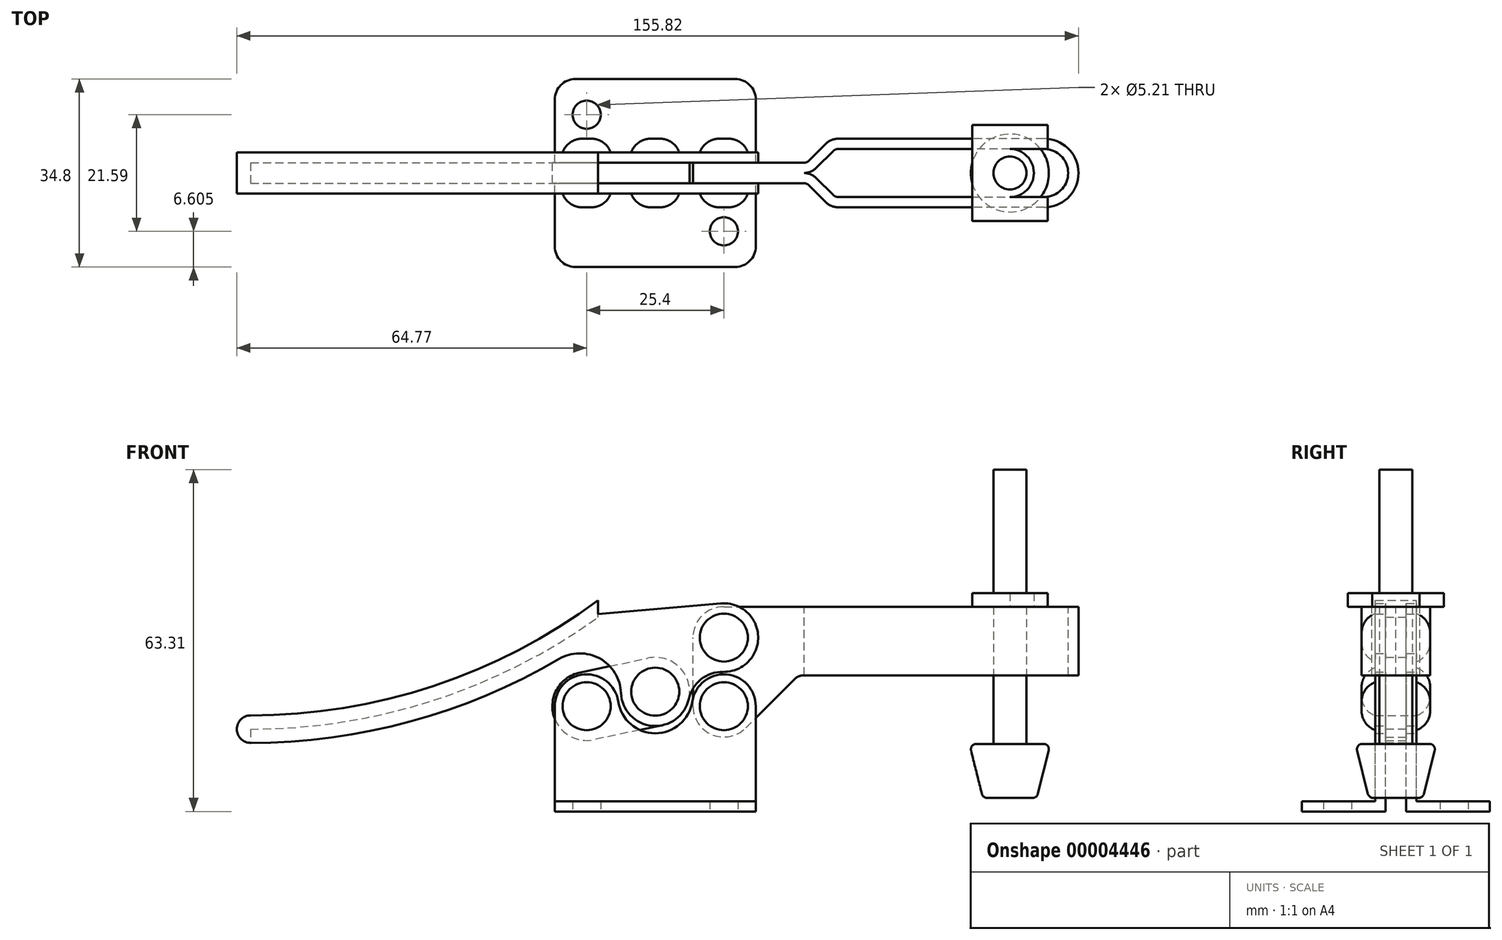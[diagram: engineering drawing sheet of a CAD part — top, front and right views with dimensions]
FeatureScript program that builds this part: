
annotation { "Feature Type Name" : "Feature", "Feature Type Description" : "" }
export const myFeature = defineFeature(function(context is Context, id is Id, definition is map)
    precondition{}
    {
        {
            var Q0;
            Q0=qCreatedBy(makeId("Front.planeOp"),FACE);
            var sketch = newSketch(context, id + "F0", { "sketchPlane" : qUnion([Q0])});
            skLineSegment(sketch, "E0", {"start": v(0, 0) * mm, "end": v(-18.6, 0) * mm});
            skLineSegment(sketch, "E1", {"start": v(-18.6, 0) * mm, "end": v(-18.6, 19.5) * mm});
            skArc(sketch, "E2", {"start": v(-18.6, 19.5) * mm, "mid": v(-13.14, 25.38) * mm, "end": v(-6.86, 20.38) * mm});
            skArc(sketch, "E3", {"start": v(-6.86, 20.38) * mm, "mid": v(-4.52, 16.16) * mm, "end": v(0, 14.48) * mm});
            skArc(sketch, "E4.0.MirrorCS", {"start": v(6.86, 20.38) * mm, "mid": v(4.52, 16.16) * mm, "end": v(0, 14.48) * mm});
            skLineSegment(sketch, "E4.1.MirrorCS", {"start": v(0, 0) * mm, "end": v(18.6, 0) * mm});
            skLineSegment(sketch, "E4.2.MirrorCS", {"start": v(18.6, 0) * mm, "end": v(18.6, 19.5) * mm});
            skArc(sketch, "E4.3.MirrorCS", {"start": v(18.6, 19.5) * mm, "mid": v(13.14, 25.38) * mm, "end": v(6.86, 20.38) * mm});
            skCircle(sketch, "E5", {"center": v(-12.7, 19.5) * mm, "radius": 3.81 * mm});
            skCircle(sketch, "E6.0.MirrorC", {"center": v(12.7, 19.5) * mm, "radius": 3.81 * mm});
            skLineSegment(sketch, "E7", {"start": v(-18.6, 1.9) * mm, "end": v(18.6, 1.9) * mm});
            skSolve(sketch);
        }
        {
            var Q0;
            Q0 = qSketchRegion(id + "F0", true);
            extrude(context, id + "F1", {"entities" : qUnion([Q0]), "endBound" : BoundingType.SYMMETRIC, "depth" : 7.62 * mm});
        }
        {
            var Q0;
            {var subQ2=sQuery(id+"F0.wireOp",EDGE,"E0");Q0=makeQuery(id+"F0.imprint","IMPRINT",FACE,{"disambiguationData":[TD([[makeQuery(id+"F0.imprint","IMPRINT",EDGE,{"derivedFrom":subQ2}),-1.0]])]});}
            extrude(context, id + "F2", {"entities" : qUnion([Q0]), "operationType" : NewBodyOperationType.ADD, "endBound" : BoundingType.SYMMETRIC, "depth" : 34.8 * mm});
        }
        {
            var Q0;
            Q0 = qSketchRegion(id + "F0", true);
            extrude(context, id + "F3", {"entities" : qUnion([Q0]), "operationType" : NewBodyOperationType.REMOVE, "endBound" : BoundingType.SYMMETRIC, "oppositeDirection" : true, "depth" : 3.8 * mm});
        }
        {
            var Q0;
            Q0=qCreatedBy(makeId("Top.planeOp"),FACE);
            var sketch = newSketch(context, id + "F4", { "sketchPlane" : qUnion([Q0])});
            skCircle(sketch, "E8", {"center": v(-12.7, 10.8) * mm, "radius": 2.6 * mm});
            skArc(sketch, "E9", {"start": v(-14.8, 17.4) * mm, "mid": v(-17.49, 16.28) * mm, "end": v(-18.6, 13.59) * mm});
            skLineSegment(sketch, "E10", {"start": v(-18.6, 13.59) * mm, "end": v(-18.6, 17.4) * mm});
            skLineSegment(sketch, "E11", {"start": v(-18.6, 17.4) * mm, "end": v(-14.8, 17.4) * mm});
            skCircle(sketch, "E12.0.MirrorC", {"center": v(12.7, 10.8) * mm, "radius": 2.6 * mm});
            skLineSegment(sketch, "E12.1.MirrorCS", {"start": v(18.6, 17.4) * mm, "end": v(14.8, 17.4) * mm});
            skLineSegment(sketch, "E12.2.MirrorCS", {"start": v(18.6, 13.59) * mm, "end": v(18.6, 17.4) * mm});
            skArc(sketch, "E12.3.MirrorCS", {"start": v(14.8, 17.4) * mm, "mid": v(17.49, 16.28) * mm, "end": v(18.6, 13.59) * mm});
            skLineSegment(sketch, "E13.0.MirrorCS", {"start": v(-18.6, -13.59) * mm, "end": v(-18.6, -17.4) * mm});
            skArc(sketch, "E13.1.MirrorCS", {"start": v(-14.8, -17.4) * mm, "mid": v(-17.49, -16.28) * mm, "end": v(-18.6, -13.59) * mm});
            skCircle(sketch, "E13.2.MirrorC", {"center": v(12.7, -10.8) * mm, "radius": 2.6 * mm});
            skCircle(sketch, "E13.3.MirrorC", {"center": v(-12.7, -10.8) * mm, "radius": 2.6 * mm});
            skArc(sketch, "E13.4.MirrorCS", {"start": v(14.8, -17.4) * mm, "mid": v(17.49, -16.28) * mm, "end": v(18.6, -13.59) * mm});
            skLineSegment(sketch, "E13.5.MirrorCS", {"start": v(-18.6, -17.4) * mm, "end": v(-14.8, -17.4) * mm});
            skLineSegment(sketch, "E13.6.MirrorCS", {"start": v(18.6, -17.4) * mm, "end": v(14.8, -17.4) * mm});
            skLineSegment(sketch, "E13.7.MirrorCS", {"start": v(18.6, -13.59) * mm, "end": v(18.6, -17.4) * mm});
            skSolve(sketch);
        }
        {
            var Q0;
            Q0=makeQuery(id+"F4.imprint","IMPRINT",FACE,{"disambiguationData":[TD([[makeQuery(id+"F4.imprint","IMPRINT",EDGE,{"derivedFrom":sQuery(id+"F4.wireOp",EDGE,"E8")}),1.0]])]});
            var Q1;
            Q1=makeQuery(id+"F4.imprint","IMPRINT",FACE,{"disambiguationData":[TD([[makeQuery(id+"F4.imprint","IMPRINT",EDGE,{"derivedFrom":sQuery(id+"F4.wireOp",EDGE,"E9")}),-1.0]])]});
            var Q2;
            Q2=makeQuery(id+"F4.imprint","IMPRINT",FACE,{"disambiguationData":[TD([[makeQuery(id+"F4.imprint","IMPRINT",EDGE,{"derivedFrom":sQuery(id+"F4.wireOp",EDGE,"E12.0.MirrorC")}),-1.0]])]});
            var Q3;
            Q3=makeQuery(id+"F4.imprint","IMPRINT",FACE,{"disambiguationData":[TD([[makeQuery(id+"F4.imprint","IMPRINT",EDGE,{"derivedFrom":sQuery(id+"F4.wireOp",EDGE,"E12.1.MirrorCS")}),1.0]])]});
            var Q4;
            Q4=makeQuery(id+"F4.imprint","IMPRINT",FACE,{"disambiguationData":[TD([[makeQuery(id+"F4.imprint","IMPRINT",EDGE,{"derivedFrom":sQuery(id+"F4.wireOp",EDGE,"E13.2.MirrorC")}),1.0]])]});
            var Q5;
            Q5=makeQuery(id+"F4.imprint","IMPRINT",FACE,{"disambiguationData":[TD([[makeQuery(id+"F4.imprint","IMPRINT",EDGE,{"derivedFrom":sQuery(id+"F4.wireOp",EDGE,"E13.4.MirrorCS")}),-1.0]])]});
            var Q6;
            Q6=makeQuery(id+"F4.imprint","IMPRINT",FACE,{"disambiguationData":[TD([[makeQuery(id+"F4.imprint","IMPRINT",EDGE,{"derivedFrom":sQuery(id+"F4.wireOp",EDGE,"E13.0.MirrorCS")}),1.0]])]});
            var Q7;
            Q7=makeQuery(id+"F4.imprint","IMPRINT",FACE,{"disambiguationData":[TD([[makeQuery(id+"F4.imprint","IMPRINT",EDGE,{"derivedFrom":sQuery(id+"F4.wireOp",EDGE,"E13.3.MirrorC")}),-1.0]])]});
            extrude(context, id + "F5", {"entities" : qUnion([Q0, Q1, Q2, Q3, Q4, Q5, Q6, Q7]), "operationType" : NewBodyOperationType.REMOVE, "endBound" : BoundingType.THROUGH_ALL, "depth" : 25.4 * mm});
        }
        {
            var Q0;
            Q0=qCreatedBy(makeId("Front.planeOp"),FACE);
            var sketch = newSketch(context, id + "F6", { "sketchPlane" : qUnion([Q0])});
            skCircle(sketch, "E14", {"center": v(12.7, 19.5) * mm, "radius": 5.72 * mm});
            skLineSegment(sketch, "E15", {"start": v(6.98, 19.5) * mm, "end": v(6.98, 32.2) * mm});
            skCircle(sketch, "E16", {"center": v(12.7, 32.2) * mm, "radius": 5.72 * mm});
            skLineSegment(sketch, "E17", {"start": v(12.7, 37.9) * mm, "end": v(75.8, 37.9) * mm});
            skLineSegment(sketch, "E18", {"start": v(16.74, 15.45) * mm, "end": v(25.75, 24.47) * mm});
            skArc(sketch, "E19", {"start": v(25.75, 24.47) * mm, "mid": v(26.58, 25.02) * mm, "end": v(27.55, 25.2) * mm});
            skLineSegment(sketch, "E20", {"start": v(27.55, 25.2) * mm, "end": v(75.8, 25.2) * mm});
            skLineSegment(sketch, "E21", {"start": v(27.55, 25.2) * mm, "end": v(27.55, 37.9) * mm});
            skArc(sketch, "E22", {"start": v(75.8, 25.2) * mm, "mid": v(77.6, 25.95) * mm, "end": v(78.35, 27.75) * mm});
            skArc(sketch, "E23", {"start": v(75.8, 37.9) * mm, "mid": v(77.6, 37.17) * mm, "end": v(78.35, 35.37) * mm});
            skLineSegment(sketch, "E24", {"start": v(78.35, 35.37) * mm, "end": v(78.35, 27.75) * mm});
            skCircle(sketch, "E25", {"center": v(-12.7, 19.5) * mm, "radius": 3.81 * mm});
            skCircle(sketch, "E26", {"center": v(0, 22.18) * mm, "radius": 3.81 * mm});
            skCircle(sketch, "E27", {"center": v(-12.7, 19.5) * mm, "radius": 6.35 * mm});
            skCircle(sketch, "E28", {"center": v(0, 22.18) * mm, "radius": 6.35 * mm});
            skLineSegment(sketch, "E29", {"start": v(-14.01, 25.7) * mm, "end": v(-1.31, 28.4) * mm});
            skLineSegment(sketch, "E30", {"start": v(1.31, 15.97) * mm, "end": v(-11.39, 13.28) * mm});
            skSolve(sketch);
        }
        {
            var Q0;
            {var subQ0=sQuery(id+"F6.wireOp",EDGE,"E14");var subQ2=makeQuery(id+"F6.imprint","INTERSECT",VERTEX,{"derivedFrom":[subQ0,sQuery(id+"F6.wireOp",EDGE,"E15")]});Q0=makeQuery(id+"F6.imprint","IMPRINT",FACE,{"disambiguationData":[TD([[makeQuery(id+"F6.imprint","IMPRINT",EDGE,{"disambiguationData":[TD([[subQ2,-1.0]])],"derivedFrom":subQ0}),1.0]])]});}
            var Q1;
            {var subQ0=sQuery(id+"F6.wireOp",EDGE,"E16");var subQ2=makeQuery(id+"F6.imprint","INTERSECT",VERTEX,{"derivedFrom":[sQuery(id+"F6.wireOp",EDGE,"E15"),subQ0]});Q1=makeQuery(id+"F6.imprint","IMPRINT",FACE,{"disambiguationData":[TD([[makeQuery(id+"F6.imprint","IMPRINT",EDGE,{"disambiguationData":[TD([[subQ2,1.0]])],"derivedFrom":subQ0}),1.0]])]});}
            var Q2;
            {var subQ5=sQuery(id+"F6.wireOp",EDGE,"E15");Q2=makeQuery(id+"F6.imprint","IMPRINT",FACE,{"disambiguationData":[TD([[makeQuery(id+"F6.imprint","IMPRINT",EDGE,{"derivedFrom":subQ5}),-1.0]])]});}
            var Q3;
            {var subQ1=sQuery(id+"F6.wireOp",EDGE,"E29");Q3=makeQuery(id+"F6.imprint","IMPRINT",FACE,{"disambiguationData":[TD([[makeQuery(id+"F6.imprint","IMPRINT",EDGE,{"derivedFrom":subQ1}),-1.0]])]});}
            var Q4;
            Q4=makeQuery(id+"F6.imprint","IMPRINT",FACE,{"disambiguationData":[TD([[makeQuery(id+"F6.imprint","IMPRINT",EDGE,{"derivedFrom":sQuery(id+"F6.wireOp",EDGE,"E26")}),-1.0]])]});
            var Q5;
            Q5=makeQuery(id+"F6.imprint","IMPRINT",FACE,{"disambiguationData":[TD([[makeQuery(id+"F6.imprint","IMPRINT",EDGE,{"derivedFrom":sQuery(id+"F6.wireOp",EDGE,"E25")}),-1.0]])]});
            extrude(context, id + "F7", {"entities" : qUnion([Q0, Q1, Q2, Q3, Q4, Q5]), "operationType" : NewBodyOperationType.ADD, "endBound" : BoundingType.SYMMETRIC, "depth" : 3.8 * mm});
        }
        {
            var Q0;
            Q0=makeQuery(id+"F7.opExtrude","SWEPT_FACE",FACE,{"disambiguationData":[OSD([sQuery(id+"F6.wireOp",EDGE,"E17")])]});
            var sketch = newSketch(context, id + "F8", { "sketchPlane" : qUnion([Q0])});
            skLineSegment(sketch, "E31", {"start": v(12.7, 1.9) * mm, "end": v(27.55, 1.9) * mm});
            skArc(sketch, "E32", {"start": v(27.55, 1.9) * mm, "mid": v(28.04, 2) * mm, "end": v(28.45, 2.28) * mm});
            skLineSegment(sketch, "E33", {"start": v(27.55, 0) * mm, "end": v(12.7, 0) * mm});
            skArc(sketch, "E34", {"start": v(27.55, 0) * mm, "mid": v(28.76, 0.24) * mm, "end": v(29.8, 0.93) * mm});
            skLineSegment(sketch, "E35", {"start": v(28.45, 2.28) * mm, "end": v(31.6, 5.42) * mm});
            skLineSegment(sketch, "E36", {"start": v(29.8, 0.93) * mm, "end": v(32.94, 4.07) * mm});
            skLineSegment(sketch, "E37", {"start": v(33.84, 4.44) * mm, "end": v(72, 4.44) * mm});
            skLineSegment(sketch, "E38", {"start": v(72, 6.35) * mm, "end": v(33.84, 6.35) * mm});
            skArc(sketch, "E39", {"start": v(32.94, 4.07) * mm, "mid": v(33.35, 4.35) * mm, "end": v(33.84, 4.44) * mm});
            skArc(sketch, "E40", {"start": v(31.6, 5.42) * mm, "mid": v(32.62, 6.1) * mm, "end": v(33.84, 6.35) * mm});
            skArc(sketch, "E41", {"start": v(72, 4.44) * mm, "mid": v(75.14, 3.14) * mm, "end": v(76.44, 0) * mm});
            skArc(sketch, "E42", {"start": v(72, 6.35) * mm, "mid": v(76.49, 4.5) * mm, "end": v(78.35, 0) * mm});
            skLineSegment(sketch, "E43", {"start": v(76.44, 0) * mm, "end": v(78.35, 0) * mm});
            skArc(sketch, "E44.0.MirrorCS", {"start": v(72, -4.45) * mm, "mid": v(75.14, -3.14) * mm, "end": v(76.44, 0) * mm});
            skArc(sketch, "E44.1.MirrorCS", {"start": v(31.6, -5.42) * mm, "mid": v(32.62, -6.1) * mm, "end": v(33.84, -6.35) * mm});
            skLineSegment(sketch, "E44.3.MirrorCS", {"start": v(29.8, -0.93) * mm, "end": v(32.94, -4.07) * mm});
            skArc(sketch, "E44.4.MirrorCS", {"start": v(72, -6.35) * mm, "mid": v(76.49, -4.5) * mm, "end": v(78.35, 0) * mm});
            skArc(sketch, "E44.5.MirrorCS", {"start": v(27.55, -1.9) * mm, "mid": v(28.04, -2) * mm, "end": v(28.45, -2.28) * mm});
            skLineSegment(sketch, "E44.6.MirrorCS", {"start": v(33.84, -4.44) * mm, "end": v(72, -4.44) * mm});
            skLineSegment(sketch, "E44.7.MirrorCS", {"start": v(72, -6.35) * mm, "end": v(33.84, -6.35) * mm});
            skLineSegment(sketch, "E44.8.MirrorCS", {"start": v(28.45, -2.28) * mm, "end": v(31.6, -5.42) * mm});
            skArc(sketch, "E44.9.MirrorCS", {"start": v(32.94, -4.07) * mm, "mid": v(33.35, -4.35) * mm, "end": v(33.84, -4.44) * mm});
            skArc(sketch, "E44.10.MirrorCS", {"start": v(27.55, 0) * mm, "mid": v(28.76, -0.24) * mm, "end": v(29.8, -0.93) * mm});
            skSolve(sketch);
        }
        {
            var Q0;
            Q0=makeQuery(id+"F8.imprint","IMPRINT",FACE,{"disambiguationData":[TD([[makeQuery(id+"F8.imprint","IMPRINT",EDGE,{"derivedFrom":sQuery(id+"F8.wireOp",EDGE,"E44.0.MirrorCS")}),-1.0]])]});
            var Q1;
            {var subQ2=sQuery(id+"F8.wireOp",EDGE,"E32");Q1=makeQuery(id+"F8.imprint","IMPRINT",FACE,{"disambiguationData":[TD([[makeQuery(id+"F8.imprint","IMPRINT",EDGE,{"derivedFrom":subQ2}),-1.0]])]});}
            var Q2;
            Q2=makeQuery(id+"F8.imprint","IMPRINT",FACE,{"disambiguationData":[TD([[makeQuery(id+"F8.imprint","IMPRINT",EDGE,{"derivedFrom":sQuery(id+"F8.wireOp",EDGE,"E34")}),-1.0]])]});
            extrude(context, id + "F9", {"entities" : qUnion([Q0, Q1, Q2]), "operationType" : NewBodyOperationType.ADD, "oppositeDirection" : true, "depth" : 12.7 * mm});
        }
        {
            var Q0;
            Q0=makeQuery(id+"F8.imprint","IMPRINT",FACE,{"disambiguationData":[TD([[makeQuery(id+"F8.imprint","IMPRINT",EDGE,{"derivedFrom":sQuery(id+"F8.wireOp",EDGE,"E34")}),-1.0]])]});
            extrude(context, id + "F10", {"entities" : qUnion([Q0]), "operationType" : NewBodyOperationType.REMOVE, "endBound" : BoundingType.THROUGH_ALL, "oppositeDirection" : true, "depth" : 25.4 * mm});
        }
        {
            var Q0;
            Q0=qCreatedBy(makeId("Front.planeOp"),FACE);
            var sketch = newSketch(context, id + "F11", { "sketchPlane" : qUnion([Q0])});
            skCircle(sketch, "E45", {"center": v(12.7, 32.2) * mm, "radius": 6.35 * mm});
            skCircle(sketch, "E46", {"center": v(0, 22.18) * mm, "radius": 6.35 * mm});
            skArc(sketch, "E47", {"start": v(12.56, 25.85) * mm, "mid": v(8.48, 24.48) * mm, "end": v(6.2, 20.84) * mm});
            skArc(sketch, "E48", {"start": v(-6.35, 21.94) * mm, "mid": v(-10.3, 28.33) * mm, "end": v(-17.82, 28.22) * mm});
            skArc(sketch, "E49", {"start": v(-17.82, 28.22) * mm, "mid": v(-45.34, 16.65) * mm, "end": v(-74.93, 12.7) * mm});
            skArc(sketch, "E50", {"start": v(-74.93, 12.7) * mm, "mid": v(-77.47, 15.24) * mm, "end": v(-74.93, 17.78) * mm});
            skArc(sketch, "E51", {"start": v(-74.93, 17.78) * mm, "mid": v(-41.06, 23.24) * mm, "end": v(-10.63, 39.07) * mm});
            skLineSegment(sketch, "E52", {"start": v(12.15, 38.52) * mm, "end": v(-10.63, 36.53) * mm});
            skLineSegment(sketch, "E53", {"start": v(-10.63, 36.53) * mm, "end": v(-10.63, 39.07) * mm});
            skArc(sketch, "E54", {"start": v(-74.93, 15.24) * mm, "mid": v(-41.16, 20.54) * mm, "end": v(-10.63, 35.92) * mm});
            skLineSegment(sketch, "E55", {"start": v(-10.63, 36.53) * mm, "end": v(-10.63, 35.92) * mm});
            skLineSegment(sketch, "E56", {"start": v(-74.93, 15.24) * mm, "end": v(-74.93, 17.78) * mm});
            skLineSegment(sketch, "E57", {"start": v(6.33, 22.73) * mm, "end": v(5, 37.9) * mm});
            skLineSegment(sketch, "E58", {"start": v(15.47, 37.9) * mm, "end": v(12.7, 37.9) * mm});
            skLineSegment(sketch, "E59", {"start": v(6.98, 29.43) * mm, "end": v(6.98, 32.2) * mm});
            skArc(sketch, "E60", {"start": v(12.7, 37.9) * mm, "mid": v(8.66, 36.24) * mm, "end": v(6.99, 32.2) * mm});
            skLineSegment(sketch, "E61", {"start": v(6.98, 29.43) * mm, "end": v(6.98, 22.8) * mm});
            skSolve(sketch);
        }
        {
            var Q0;
            {var subQ0=sQuery(id+"F11.wireOp",EDGE,"E46");var subQ3=makeQuery(id+"F11.imprint","INTERSECT",VERTEX,{"derivedFrom":[subQ0,sQuery(id+"F11.wireOp",EDGE,"E48")]});Q0=makeQuery(id+"F11.imprint","IMPRINT",FACE,{"disambiguationData":[TD([[makeQuery(id+"F11.imprint","IMPRINT",EDGE,{"disambiguationData":[TD([[subQ3,1.0]])],"derivedFrom":subQ0}),1.0]])]});}
            var Q1;
            Q1=makeQuery(id+"F11.imprint","IMPRINT",FACE,{"disambiguationData":[TD([[makeQuery(id+"F11.imprint","IMPRINT",EDGE,{"derivedFrom":sQuery(id+"F11.wireOp",EDGE,"E51")}),-1.0]])]});
            var Q2;
            {var subQ3=sQuery(id+"F11.wireOp",EDGE,"E48");Q2=makeQuery(id+"F11.imprint","IMPRINT",FACE,{"disambiguationData":[TD([[makeQuery(id+"F11.imprint","IMPRINT",EDGE,{"derivedFrom":subQ3}),-1.0]])]});}
            var Q3;
            {var subQ0=sQuery(id+"F11.wireOp",EDGE,"E61");Q3=makeQuery(id+"F11.imprint","IMPRINT",FACE,{"disambiguationData":[TD([[makeQuery(id+"F11.imprint","IMPRINT",EDGE,{"derivedFrom":subQ0}),1.0]])]});}
            var Q4;
            {var subQ1=sQuery(id+"F11.wireOp",EDGE,"E58");Q4=makeQuery(id+"F11.imprint","IMPRINT",FACE,{"disambiguationData":[TD([[makeQuery(id+"F11.imprint","IMPRINT",EDGE,{"derivedFrom":subQ1}),1.0]])]});}
            var Q5;
            {var subQ1=sQuery(id+"F11.wireOp",EDGE,"E58");Q5=makeQuery(id+"F11.imprint","IMPRINT",FACE,{"disambiguationData":[TD([[makeQuery(id+"F11.imprint","IMPRINT",EDGE,{"derivedFrom":subQ1}),-1.0]])]});}
            var Q6;
            {var subQ1=sQuery(id+"F11.wireOp",EDGE,"E57");Q6=makeQuery(id+"F11.imprint","IMPRINT",FACE,{"disambiguationData":[TD([[makeQuery(id+"F11.imprint","IMPRINT",EDGE,{"derivedFrom":subQ1}),-1.0]])]});}
            extrude(context, id + "F12", {"entities" : qUnion([Q0, Q1, Q2, Q3, Q4, Q5, Q6]), "operationType" : NewBodyOperationType.ADD, "endBound" : BoundingType.SYMMETRIC, "depth" : 7.62 * mm});
        }
        {
            var Q0;
            Q0=qCreatedBy(makeId("Front.planeOp"),FACE);
            var sketch = newSketch(context, id + "F13", { "sketchPlane" : qUnion([Q0])});
            skCircle(sketch, "E62", {"center": v(12.7, 32.2) * mm, "radius": 4.45 * mm});
            skCircle(sketch, "E63", {"center": v(12.7, 19.5) * mm, "radius": 4.45 * mm});
            skCircle(sketch, "E64", {"center": v(0, 22.18) * mm, "radius": 4.45 * mm});
            skCircle(sketch, "E65", {"center": v(-12.7, 19.5) * mm, "radius": 4.45 * mm});
            skSolve(sketch);
        }
        {
            var Q0;
            {Q0=qUnion([makeQuery(id+"F13.imprint","IMPRINT",FACE,{"disambiguationData":[TD([[makeQuery(id+"F13.imprint","IMPRINT",EDGE,{"derivedFrom":sQuery(id+"F13.wireOp",EDGE,"E62")}),1.0]])]}),makeQuery(id+"F13.imprint","IMPRINT",FACE,{"disambiguationData":[TD([[makeQuery(id+"F13.imprint","IMPRINT",EDGE,{"derivedFrom":sQuery(id+"F13.wireOp",EDGE,"E63")}),1.0]])]}),makeQuery(id+"F13.imprint","IMPRINT",FACE,{"disambiguationData":[TD([[makeQuery(id+"F13.imprint","IMPRINT",EDGE,{"derivedFrom":sQuery(id+"F13.wireOp",EDGE,"E64")}),1.0]])]}),makeQuery(id+"F13.imprint","IMPRINT",FACE,{"disambiguationData":[TD([[makeQuery(id+"F13.imprint","IMPRINT",EDGE,{"derivedFrom":sQuery(id+"F13.wireOp",EDGE,"E65")}),1.0]])]})]);}
            extrude(context, id + "F14", {"entities" : qUnion([Q0]), "operationType" : NewBodyOperationType.ADD, "endBound" : BoundingType.SYMMETRIC, "depth" : 12.7 * mm});
        }
        {
            var Q0;
            Q0=qCreatedBy(makeId("Front.planeOp"),FACE);
            var sketch = newSketch(context, id + "F15", { "sketchPlane" : qUnion([Q0])});
            skLineSegment(sketch, "E66", {"start": v(-8.43, 26.89) * mm, "end": v(-1.31, 28.4) * mm});
            skArc(sketch, "E67", {"start": v(6.2, 20.84) * mm, "mid": v(4.5, 26.66) * mm, "end": v(-1.31, 28.4) * mm});
            skArc(sketch, "E68", {"start": v(6.98, 22.8) * mm, "mid": v(6.51, 21.85) * mm, "end": v(6.2, 20.84) * mm});
            skLineSegment(sketch, "E69", {"start": v(6.98, 22.8) * mm, "end": v(6.98, 32.2) * mm});
            skArc(sketch, "E70", {"start": v(12.7, 37.9) * mm, "mid": v(8.66, 36.24) * mm, "end": v(6.99, 32.2) * mm});
            skLineSegment(sketch, "E71", {"start": v(12.7, 37.9) * mm, "end": v(15.47, 37.9) * mm});
            skArc(sketch, "E72", {"start": v(15.47, 37.9) * mm, "mid": v(13.85, 38.44) * mm, "end": v(12.15, 38.52) * mm});
            skLineSegment(sketch, "E73", {"start": v(12.15, 38.52) * mm, "end": v(-10.63, 36.53) * mm});
            skLineSegment(sketch, "E74", {"start": v(-10.63, 35.92) * mm, "end": v(-10.63, 36.53) * mm});
            skArc(sketch, "E75", {"start": v(-8.43, 26.89) * mm, "mid": v(-12.89, 29.2) * mm, "end": v(-17.82, 28.22) * mm});
            skArc(sketch, "E76", {"start": v(-74.93, 15.24) * mm, "mid": v(-41.16, 20.54) * mm, "end": v(-10.63, 35.92) * mm});
            skArc(sketch, "E77", {"start": v(-74.93, 12.7) * mm, "mid": v(-45.34, 16.65) * mm, "end": v(-17.82, 28.22) * mm});
            skLineSegment(sketch, "E78", {"start": v(-74.93, 15.24) * mm, "end": v(-74.93, 12.7) * mm});
            skSolve(sketch);
        }
        {
            var Q0;
            Q0=makeQuery(id+"F15.imprint","IMPRINT",FACE,{"disambiguationData":[TD([[makeQuery(id+"F15.imprint","IMPRINT",EDGE,{"derivedFrom":sQuery(id+"F15.wireOp",EDGE,"E66")}),1.0]])]});
            extrude(context, id + "F16", {"entities" : qUnion([Q0]), "operationType" : NewBodyOperationType.REMOVE, "endBound" : BoundingType.SYMMETRIC, "oppositeDirection" : true, "depth" : 3.8 * mm});
        }
        {
            var Q0;
            Q0=makeQuery(id+"F14.opExtrude","CAP_FACE",FACE,{"disambiguationData":[OSD([sQuery(id+"F13.wireOp",EDGE,"E65")])],"isStart":false});
            var Q1;
            Q1=makeQuery(id+"F14.opExtrude","CAP_FACE",FACE,{"disambiguationData":[OSD([sQuery(id+"F13.wireOp",EDGE,"E64")])],"isStart":false});
            var Q2;
            Q2=makeQuery(id+"F14.opExtrude","CAP_FACE",FACE,{"disambiguationData":[OSD([sQuery(id+"F13.wireOp",EDGE,"E63")])],"isStart":false});
            var Q3;
            Q3=makeQuery(id+"F14.opExtrude","CAP_FACE",FACE,{"disambiguationData":[OSD([sQuery(id+"F13.wireOp",EDGE,"E62")])],"isStart":false});
            var Q4;
            Q4=makeQuery(id+"F14.opExtrude","CAP_FACE",FACE,{"disambiguationData":[OSD([sQuery(id+"F13.wireOp",EDGE,"E62")])],"isStart":true});
            var Q5;
            Q5=makeQuery(id+"F14.opExtrude","CAP_FACE",FACE,{"disambiguationData":[OSD([sQuery(id+"F13.wireOp",EDGE,"E63")])],"isStart":true});
            var Q6;
            Q6=makeQuery(id+"F14.opExtrude","CAP_FACE",FACE,{"disambiguationData":[OSD([sQuery(id+"F13.wireOp",EDGE,"E64")])],"isStart":true});
            var Q7;
            Q7=makeQuery(id+"F14.opExtrude","CAP_FACE",FACE,{"disambiguationData":[OSD([sQuery(id+"F13.wireOp",EDGE,"E65")])],"isStart":true});
            fillet(context, id + "F17", {"entities" : qUnion([Q0, Q1, Q2, Q3, Q4, Q5, Q6, Q7]), "radius" : 3.8 * mm, "tangentPropagation" : true, "allowEdgeOverflow" : false});
        }
        {
            var Q0;
            {var subQ0=sQuery(id+"F6.wireOp",EDGE,"E17");Q0=makeQuery(id+"F16.boolean.opBoolean","MERGE",FACE,{"derivedFrom":[makeQuery(id+"F9.boolean.opBoolean","MERGE",FACE,{"derivedFrom":[makeQuery(id+"F7.opExtrude","SWEPT_FACE",FACE,{"disambiguationData":[OSD([subQ0])]}),makeQuery(id+"F9.opExtrude","CAP_FACE",FACE,{"disambiguationData":[OSD([subQ0,sQuery(id+"F6.wireOp",EDGE,"E21"),sQuery(id+"F8.wireOp",EDGE,"E32"),sQuery(id+"F8.wireOp",EDGE,"E35"),sQuery(id+"F8.wireOp",EDGE,"E38"),sQuery(id+"F8.wireOp",EDGE,"E40"),sQuery(id+"F8.wireOp",EDGE,"E42"),sQuery(id+"F8.wireOp",EDGE,"E44.1.MirrorCS"),sQuery(id+"F8.wireOp",EDGE,"E44.4.MirrorCS"),sQuery(id+"F8.wireOp",EDGE,"E44.5.MirrorCS"),sQuery(id+"F8.wireOp",EDGE,"E44.7.MirrorCS"),sQuery(id+"F8.wireOp",EDGE,"E44.8.MirrorCS")])],"isStart":true})]}),makeQuery(id+"F16.opExtrude","SWEPT_FACE",FACE,{"disambiguationData":[OSD([sQuery(id+"F15.wireOp",EDGE,"E71")])]})]});}
            var sketch = newSketch(context, id + "F18", { "sketchPlane" : qUnion([Q0])});
            skCircle(sketch, "E79", {"center": v(65.65, 0) * mm, "radius": 4.44 * mm});
            skCircle(sketch, "E80", {"center": v(65.65, 0) * mm, "radius": 3.05 * mm});
            skLineSegment(sketch, "E81", {"start": v(65.65, -4.44) * mm, "end": v(65.65, 4.44) * mm});
            skLineSegment(sketch, "E82.rect.bottom", {"start": v(58.66, -8.89) * mm, "end": v(72.63, -8.89) * mm});
            skLineSegment(sketch, "E82.rect.top", {"start": v(58.66, 8.89) * mm, "end": v(72.63, 8.89) * mm});
            skLineSegment(sketch, "E82.rect.left", {"start": v(58.66, -8.89) * mm, "end": v(58.66, 8.89) * mm});
            skLineSegment(sketch, "E82.rect.right", {"start": v(72.63, -8.89) * mm, "end": v(72.63, 8.89) * mm});
            skSolve(sketch);
        }
        {
            var Q0;
            {var subQ0=sQuery(id+"F18.wireOp",EDGE,"E81");var subQ1=sQuery(id+"F18.wireOp",EDGE,"E80");var subQ3=makeQuery(id+"F18.imprint","INTERSECT",VERTEX,{"disambiguationData":[OD(0.0)],"derivedFrom":[subQ1,subQ0]});Q0=makeQuery(id+"F18.imprint","IMPRINT",FACE,{"disambiguationData":[TD([[makeQuery(id+"F18.imprint","IMPRINT",EDGE,{"disambiguationData":[TD([[subQ3,1.0]])],"derivedFrom":subQ1}),1.0]])]});}
            var Q1;
            {var subQ0=sQuery(id+"F18.wireOp",EDGE,"E81");var subQ1=sQuery(id+"F18.wireOp",EDGE,"E80");var subQ3=makeQuery(id+"F18.imprint","INTERSECT",VERTEX,{"disambiguationData":[OD(0.0)],"derivedFrom":[subQ1,subQ0]});Q1=makeQuery(id+"F18.imprint","IMPRINT",FACE,{"disambiguationData":[TD([[makeQuery(id+"F18.imprint","IMPRINT",EDGE,{"disambiguationData":[TD([[subQ3,-1.0]])],"derivedFrom":subQ1}),1.0]])]});}
            extrude(context, id + "F19", {"entities" : qUnion([Q0, Q1]), "operationType" : NewBodyOperationType.ADD, "endBound" : BoundingType.SYMMETRIC, "depth" : 50.8 * mm});
        }
        {
            var Q0;
            Q0=makeQuery(id+"F19.opExtrude","CAP_FACE",FACE,{"disambiguationData":[OSD([sQuery(id+"F18.wireOp",EDGE,"E80")])],"isStart":true});
            var sketch = newSketch(context, id + "F20", { "sketchPlane" : qUnion([Q0])});
            skLineSegment(sketch, "E83", {"start": v(65.65, 0) * mm, "end": v(62.6, 0) * mm});
            skSolve(sketch);
        }
        {
            var Q0;
            Q0=qCreatedBy(makeId("Front.planeOp"),FACE);
            var sketch = newSketch(context, id + "F21", { "sketchPlane" : qUnion([Q0])});
            skLineSegment(sketch, "E84", {"start": v(65.65, 12.5) * mm, "end": v(58.15, 12.5) * mm});
            skLineSegment(sketch, "E85", {"start": v(58.15, 12.5) * mm, "end": v(60.65, 2.5) * mm});
            skLineSegment(sketch, "E86", {"start": v(60.65, 2.5) * mm, "end": v(65.65, 2.5) * mm});
            skLineSegment(sketch, "E87", {"start": v(65.65, 2.5) * mm, "end": v(65.65, 12.5) * mm});
            skSolve(sketch);
        }
        {
            var Q0;
            Q0=makeQuery(id+"F21.imprint","IMPRINT",FACE,{"disambiguationData":[TD([[makeQuery(id+"F21.imprint","IMPRINT",EDGE,{"derivedFrom":sQuery(id+"F21.wireOp",EDGE,"E84")}),1.0]])]});
            var Q1;
            Q1=sQuery(id+"F21.wireOp",EDGE,"E87");
            revolve(context, id + "F22", {"operationType" : NewBodyOperationType.ADD, "entities" : qUnion([Q0]), "axis" : qUnion([Q1]), "revolveType" : RevolveType.FULL});
        }
        {
            var Q0;
            Q0=makeQuery(id+"F22.opRevolve","SWEPT_EDGE",EDGE,{"disambiguationData":[OSD([sQuery(id+"F21.wireOp",EDGE,"E84"),sQuery(id+"F21.wireOp",EDGE,"E85")])]});
            var Q1;
            Q1=makeQuery(id+"F22.opRevolve","SWEPT_EDGE",EDGE,{"disambiguationData":[OSD([sQuery(id+"F21.wireOp",EDGE,"E85"),sQuery(id+"F21.wireOp",EDGE,"E86")])]});
            fillet(context, id + "F23", {"entities" : qUnion([Q0, Q1]), "radius" : 1 * mm, "tangentPropagation" : true, "allowEdgeOverflow" : false});
        }
        {
            var Q0;
            {var subQ7=sQuery(id+"F18.wireOp",EDGE,"E82.rect.bottom");Q0=makeQuery(id+"F18.imprint","IMPRINT",FACE,{"disambiguationData":[TD([[makeQuery(id+"F18.imprint","IMPRINT",EDGE,{"derivedFrom":subQ7}),1.0]])]});}
            var Q1;
            {var subQ0=makeQuery(id+"F10.boolean.opBoolean","COPY",EDGE,{"derivedFrom":makeQuery(id+"F10.opExtrude","CAP_EDGE",EDGE,{"disambiguationData":[OSD([sQuery(id+"F8.wireOp",EDGE,"E44.6.MirrorCS")])],"isStart":true})});var subQ1=sQuery(id+"F18.wireOp",EDGE,"E82.rect.left");var subQ2=makeQuery(id+"F18.imprint","INTERSECT",VERTEX,{"derivedFrom":[subQ0,subQ1]});Q1=makeQuery(id+"F18.imprint","IMPRINT",FACE,{"disambiguationData":[TD([[makeQuery(id+"F18.imprint","IMPRINT",EDGE,{"disambiguationData":[TD([[subQ2,-1.0]])],"derivedFrom":subQ1}),-1.0]])]});}
            var Q2;
            {var subQ1=sQuery(id+"F18.wireOp",EDGE,"E82.rect.left");var subQ8=makeQuery(id+"F9.opExtrude","CAP_EDGE",EDGE,{"disambiguationData":[OSD([sQuery(id+"F8.wireOp",EDGE,"E44.7.MirrorCS")])],"isStart":true});var subQ9=makeQuery(id+"F18.imprint","INTERSECT",VERTEX,{"derivedFrom":[subQ8,subQ1]});Q2=makeQuery(id+"F18.imprint","IMPRINT",FACE,{"disambiguationData":[TD([[makeQuery(id+"F18.imprint","IMPRINT",EDGE,{"disambiguationData":[TD([[subQ9,-1.0]])],"derivedFrom":subQ1}),-1.0]])]});}
            var Q3;
            {var subQ0=makeQuery(id+"F10.boolean.opBoolean","COPY",EDGE,{"derivedFrom":makeQuery(id+"F10.opExtrude","CAP_EDGE",EDGE,{"disambiguationData":[OSD([sQuery(id+"F8.wireOp",EDGE,"E44.6.MirrorCS")])],"isStart":true})});var subQ1=sQuery(id+"F18.wireOp",EDGE,"E79");var subQ2=sQuery(id+"F18.wireOp",EDGE,"E81");var subQ3=makeQuery(id+"F18.imprint","INTERSECT",VERTEX,{"derivedFrom":[subQ0,subQ1,subQ2]});Q3=makeQuery(id+"F18.imprint","IMPRINT",FACE,{"disambiguationData":[TD([[makeQuery(id+"F18.imprint","IMPRINT",EDGE,{"disambiguationData":[TD([[subQ3,-1.0]])],"derivedFrom":subQ1}),-1.0]])]});}
            var Q4;
            {var subQ0=sQuery(id+"F18.wireOp",EDGE,"E81");var subQ1=sQuery(id+"F18.wireOp",EDGE,"E80");var subQ5=makeQuery(id+"F18.imprint","INTERSECT",VERTEX,{"disambiguationData":[OD(0.0)],"derivedFrom":[subQ1,subQ0]});Q4=makeQuery(id+"F18.imprint","IMPRINT",FACE,{"disambiguationData":[TD([[makeQuery(id+"F18.imprint","IMPRINT",EDGE,{"disambiguationData":[TD([[subQ5,-1.0]])],"derivedFrom":subQ1}),-1.0]])]});}
            var Q5;
            {var subQ0=sQuery(id+"F18.wireOp",EDGE,"E81");var subQ1=sQuery(id+"F18.wireOp",EDGE,"E80");var subQ5=makeQuery(id+"F18.imprint","INTERSECT",VERTEX,{"disambiguationData":[OD(0.0)],"derivedFrom":[subQ1,subQ0]});Q5=makeQuery(id+"F18.imprint","IMPRINT",FACE,{"disambiguationData":[TD([[makeQuery(id+"F18.imprint","IMPRINT",EDGE,{"disambiguationData":[TD([[subQ5,1.0]])],"derivedFrom":subQ1}),-1.0]])]});}
            var Q6;
            {var subQ5=sQuery(id+"F18.wireOp",EDGE,"E82.rect.left");var subQ10=makeQuery(id+"F9.opExtrude","CAP_EDGE",EDGE,{"disambiguationData":[OSD([sQuery(id+"F8.wireOp",EDGE,"E38")])],"isStart":true});var subQ12=makeQuery(id+"F18.imprint","INTERSECT",VERTEX,{"derivedFrom":[subQ10,subQ5]});Q6=makeQuery(id+"F18.imprint","IMPRINT",FACE,{"disambiguationData":[TD([[makeQuery(id+"F18.imprint","IMPRINT",EDGE,{"disambiguationData":[TD([[subQ12,1.0]])],"derivedFrom":subQ5}),-1.0]])]});}
            var Q7;
            {var subQ7=sQuery(id+"F18.wireOp",EDGE,"E82.rect.top");Q7=makeQuery(id+"F18.imprint","IMPRINT",FACE,{"disambiguationData":[TD([[makeQuery(id+"F18.imprint","IMPRINT",EDGE,{"derivedFrom":subQ7}),-1.0]])]});}
            extrude(context, id + "F24", {"entities" : qUnion([Q0, Q1, Q2, Q3, Q4, Q5, Q6, Q7]), "operationType" : NewBodyOperationType.ADD, "depth" : 2.54 * mm});
        }
    });
